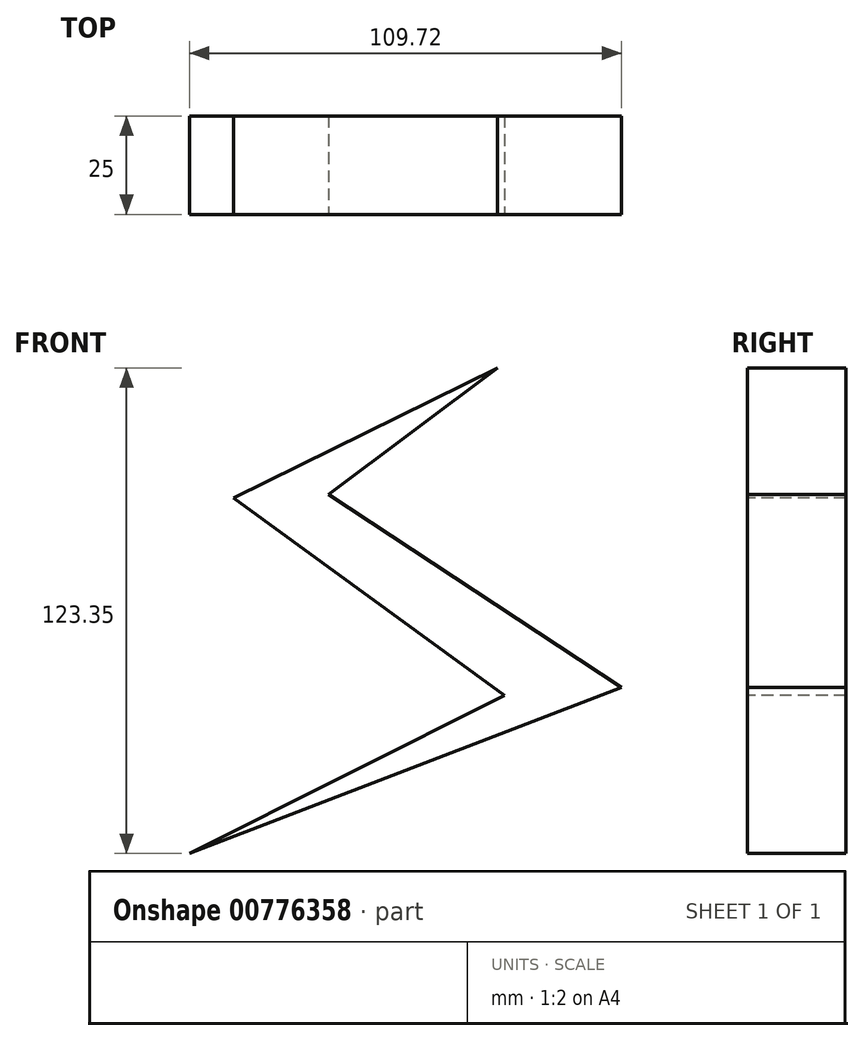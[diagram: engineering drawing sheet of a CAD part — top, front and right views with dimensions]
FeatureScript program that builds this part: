
annotation { "Feature Type Name" : "Feature", "Feature Type Description" : "" }
export const myFeature = defineFeature(function(context is Context, id is Id, definition is map)
    precondition{}
    {
        {
            var Q0;
            Q0=qCreatedBy(makeId("Front.planeOp"),FACE);
            var sketch = newSketch(context, id + "F0", { "sketchPlane" : qUnion([Q0])});
            skLineSegment(sketch, "E0", {"start": v(8.68, 62.8) * mm, "end": v(-58.32, 29.76) * mm});
            skLineSegment(sketch, "E1", {"start": v(-58.32, 29.76) * mm, "end": v(10.54, -20.43) * mm});
            skLineSegment(sketch, "E2", {"start": v(10.54, -20.43) * mm, "end": v(-69.51, -60.56) * mm});
            skLineSegment(sketch, "E3", {"start": v(8.68, 62.8) * mm, "end": v(-34.24, 30.7) * mm});
            skLineSegment(sketch, "E4", {"start": v(-34.24, 30.7) * mm, "end": v(40.21, -18.38) * mm});
            skLineSegment(sketch, "E5", {"start": v(40.21, -18.38) * mm, "end": v(-69.51, -60.56) * mm});
            skSolve(sketch);
        }
        {
            var Q0;
            Q0 = qSketchRegion(id + "F0", true);
            extrude(context, id + "F1", {"entities" : qUnion([Q0]), "oppositeDirection" : true, "depth" : 25 * mm, "offsetDistance" : 25 * mm});
        }
    });
